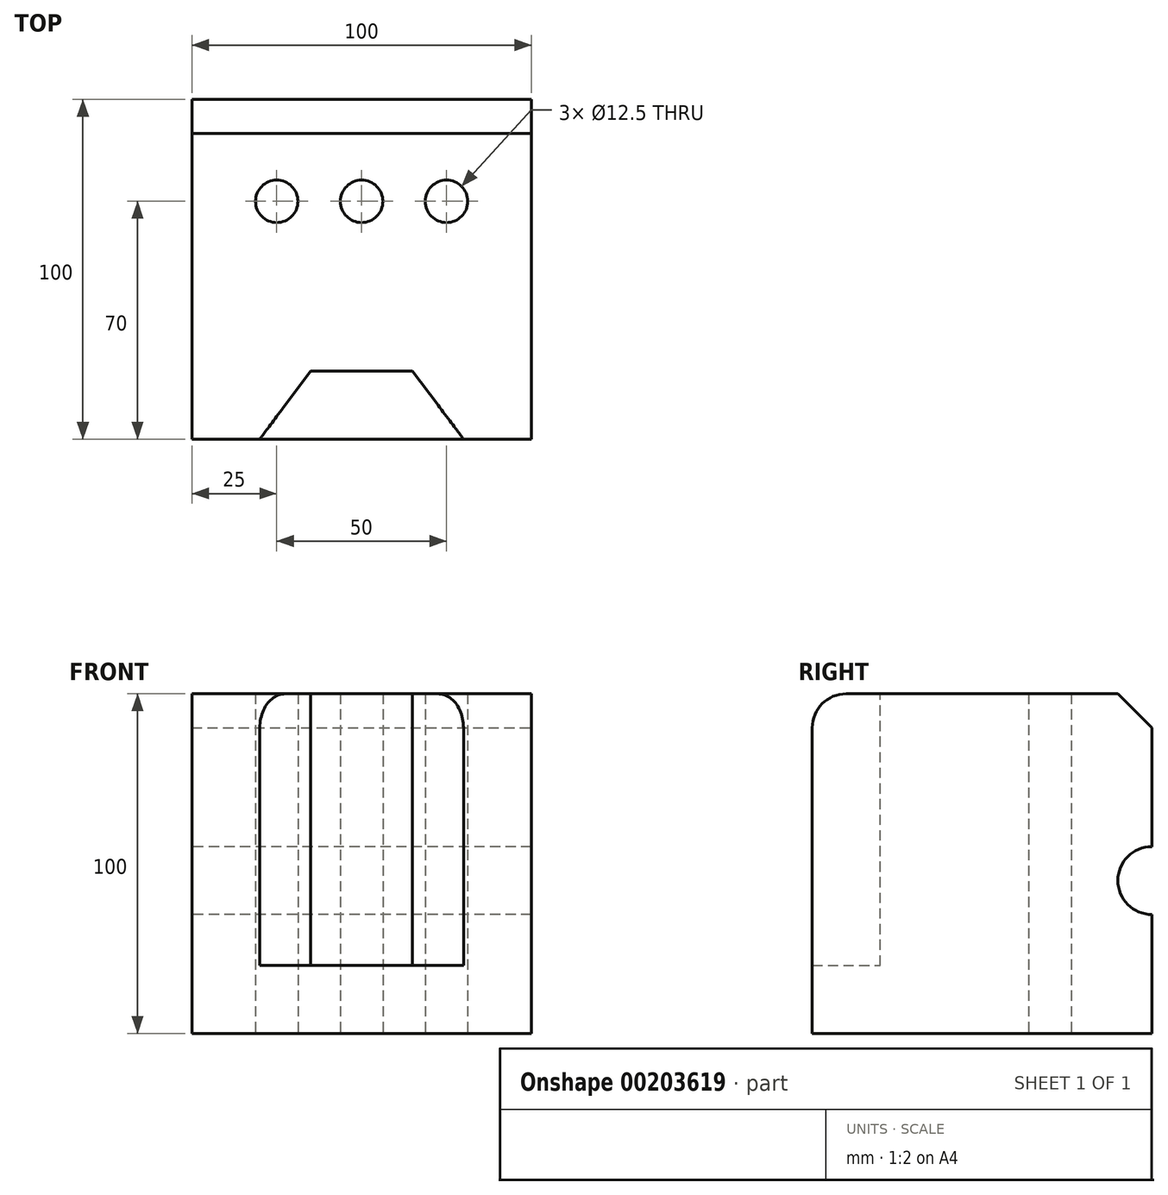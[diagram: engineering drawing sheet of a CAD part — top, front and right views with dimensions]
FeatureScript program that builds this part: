
annotation { "Feature Type Name" : "Feature", "Feature Type Description" : "" }
export const myFeature = defineFeature(function(context is Context, id is Id, definition is map)
    precondition{}
    {
        {
            var Q0;
            Q0=qCreatedBy(makeId("Top.planeOp"),FACE);
            var sketch = newSketch(context, id + "F0", { "sketchPlane" : qUnion([Q0])});
            skLineSegment(sketch, "E0.bottom", {"start": v(0, 0) * mm, "end": v(100, 0) * mm});
            skLineSegment(sketch, "E0.top", {"start": v(0, -100) * mm, "end": v(100, -100) * mm});
            skLineSegment(sketch, "E0.left", {"start": v(0, 0) * mm, "end": v(0, -100) * mm});
            skLineSegment(sketch, "E0.right", {"start": v(100, 0) * mm, "end": v(100, -100) * mm});
            skCircle(sketch, "E1", {"center": v(25, -30) * mm, "radius": 6.25 * mm});
            skCircle(sketch, "E2.1.0.0", {"center": v(50, -30) * mm, "radius": 6.25 * mm});
            skCircle(sketch, "E2.2.0.0", {"center": v(75, -30) * mm, "radius": 6.25 * mm});
            skSolve(sketch);
        }
        {
            var Q0;
            Q0=makeQuery(id+"F0.imprint","IMPRINT",FACE,{"disambiguationData":[TD([[makeQuery(id+"F0.imprint","IMPRINT",EDGE,{"derivedFrom":sQuery(id+"F0.wireOp",EDGE,"E0.bottom")}),-1.0]])]});
            extrude(context, id + "F1", {"entities" : qUnion([Q0]), "depth" : 100 * mm});
        }
        {
            var Q0;
            Q0=makeQuery(id+"F1.opExtrude","CAP_FACE",FACE,{"disambiguationData":[OSD([sQuery(id+"F0.wireOp",EDGE,"E0.bottom"),sQuery(id+"F0.wireOp",EDGE,"E0.top"),sQuery(id+"F0.wireOp",EDGE,"E0.left"),sQuery(id+"F0.wireOp",EDGE,"E0.right"),sQuery(id+"F0.wireOp",EDGE,"E1"),sQuery(id+"F0.wireOp",EDGE,"E2.1.0.0"),sQuery(id+"F0.wireOp",EDGE,"E2.2.0.0")])],"isStart":false});
            var sketch = newSketch(context, id + "F2", { "sketchPlane" : qUnion([Q0])});
            skLineSegment(sketch, "E3", {"start": v(20, -100) * mm, "end": v(35, -80) * mm});
            skLineSegment(sketch, "E4", {"start": v(35, -80) * mm, "end": v(65, -80) * mm});
            skLineSegment(sketch, "E5", {"start": v(65, -80) * mm, "end": v(80, -100) * mm});
            skSolve(sketch);
        }
        {
            var Q0;
            {var subQ0=sQuery(id+"F2.wireOp",EDGE,"E3");Q0=makeQuery(id+"F2.imprint","IMPRINT",FACE,{"disambiguationData":[TD([[makeQuery(id+"F2.imprint","IMPRINT",EDGE,{"derivedFrom":subQ0}),-1.0]])]});}
            extrude(context, id + "F3", {"entities" : qUnion([Q0]), "operationType" : NewBodyOperationType.REMOVE, "oppositeDirection" : true, "depth" : 80 * mm});
        }
        {
            var Q0;
            Q0=makeQuery(id+"F1.opExtrude","SWEPT_FACE",FACE,{"disambiguationData":[OSD([sQuery(id+"F0.wireOp",EDGE,"E0.left")])]});
            var sketch = newSketch(context, id + "F4", { "sketchPlane" : qUnion([Q0])});
            skArc(sketch, "E6", {"start": v(0, 35) * mm, "mid": v(10, 45) * mm, "end": v(0, 55) * mm});
            skSolve(sketch);
        }
        {
            var Q0;
            {var subQ0=sQuery(id+"F4.wireOp",EDGE,"E6");Q0=makeQuery(id+"F4.imprint","IMPRINT",FACE,{"disambiguationData":[TD([[makeQuery(id+"F4.imprint","IMPRINT",EDGE,{"derivedFrom":subQ0}),1.0]])]});}
            extrude(context, id + "F5", {"entities" : qUnion([Q0]), "operationType" : NewBodyOperationType.REMOVE, "oppositeDirection" : true, "depth" : 100 * mm});
        }
        {
            var Q0;
            Q0=makeQuery(id+"F1.opExtrude","CAP_EDGE",EDGE,{"disambiguationData":[OSD([sQuery(id+"F0.wireOp",EDGE,"E0.bottom")])],"isStart":false});
            chamfer(context, id + "F6", {"entities" : qUnion([Q0]), "width" : 10 * mm, "tangentPropagation" : true});
        }
        {
            var Q0;
            {var subQ0=sQuery(id+"F0.wireOp",EDGE,"E0.left");var subQ1=sQuery(id+"F0.wireOp",EDGE,"E0.top");Q0=makeQuery(id+"F3.boolean.opBoolean","SPLIT",EDGE,{"disambiguationData":[TD([makeQuery(id+"F1.opExtrude","SWEPT_FACE",FACE,{"disambiguationData":[OSD([subQ0])]})])],"derivedFrom":makeQuery(id+"F1.opExtrude","CAP_EDGE",EDGE,{"disambiguationData":[OSD([subQ1])],"isStart":false})});}
            var Q1;
            {var subQ0=sQuery(id+"F0.wireOp",EDGE,"E0.right");var subQ1=sQuery(id+"F0.wireOp",EDGE,"E0.top");Q1=makeQuery(id+"F3.boolean.opBoolean","SPLIT",EDGE,{"disambiguationData":[TD([makeQuery(id+"F1.opExtrude","SWEPT_FACE",FACE,{"disambiguationData":[OSD([subQ0])]})])],"derivedFrom":makeQuery(id+"F1.opExtrude","CAP_EDGE",EDGE,{"disambiguationData":[OSD([subQ1])],"isStart":false})});}
            fillet(context, id + "F7", {"entities" : qUnion([Q0, Q1]), "radius" : 10 * mm, "tangentPropagation" : true, "allowEdgeOverflow" : false});
        }
    });
